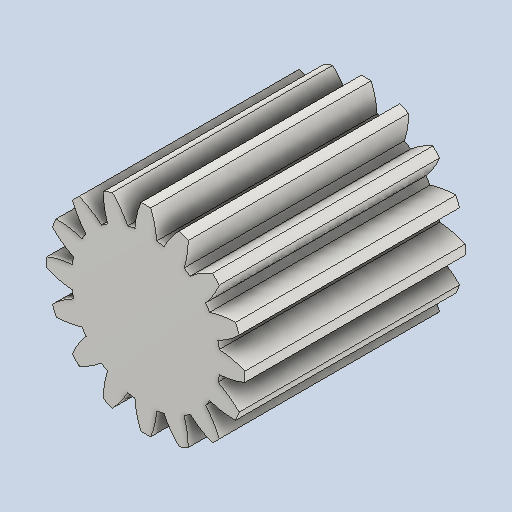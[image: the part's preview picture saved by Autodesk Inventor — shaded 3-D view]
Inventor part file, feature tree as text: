
AUTODESK INVENTOR PART (.ipt)
format: ipt  version: 2023 (Build 270158000, 158)  size: 251,904 bytes
history: native  units: mm (DEFAULTED — no unit token found)
features: plane x3, other x3, sketch x2, extrude x1
ambient origin geometry x8: Origin, YZ Plane, XZ Plane, XY Plane, X Axis, Y Axis, Z Axis, Center Point
bodies: Solid1 (feature_tree)
feature tree (9):
  extrude  "Extrusion1"  Depth=25.4mm TaperAngle=0.0deg
  plane  "Work Plane1"
  plane  "Work Plane2"
  plane  "Work Plane3"
  other  "Spur Gear"
  sketch  "Sketch1"  dims[d0=22.86mm d1=25.4mm d2=0.0mm]
  sketch  "Sketch2"  dims[d3=20.32mm d4=76.2mm d5=0.0mm d6=0.0mm d7=1.963495mm d9=0.0mm d14=0.0mm d15=27.305mm d16=0.0mm d17=0.0mm d18=0.0mm d19=27.305mm]
  other  "Srf1"
  other  "Pitch Diameter"
